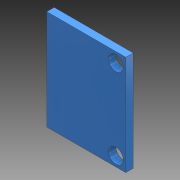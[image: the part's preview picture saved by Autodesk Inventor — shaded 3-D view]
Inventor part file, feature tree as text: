
AUTODESK INVENTOR PART (.ipt)
format: ipt  version: 2017 (Build 210142000, 142)  size: 86,016 bytes
history: native  units: mm
features: extrude x1, sketch x1
ambient origin geometry x8: Origin, YZ Plane, XZ Plane, XY Plane, X Axis, Y Axis, Z Axis, Center Point
bodies: Solid1 (feature_tree)
feature tree (2):
  extrude  "Extrusion1"  Depth=16.0mm
  sketch  "Sketch1"  dims[d0=20.26mm d1=16.0mm d2=3.0mm d3=2.0mm d4=2.0mm d5=2.0mm d6=1.5mm d7=0.0mm]
